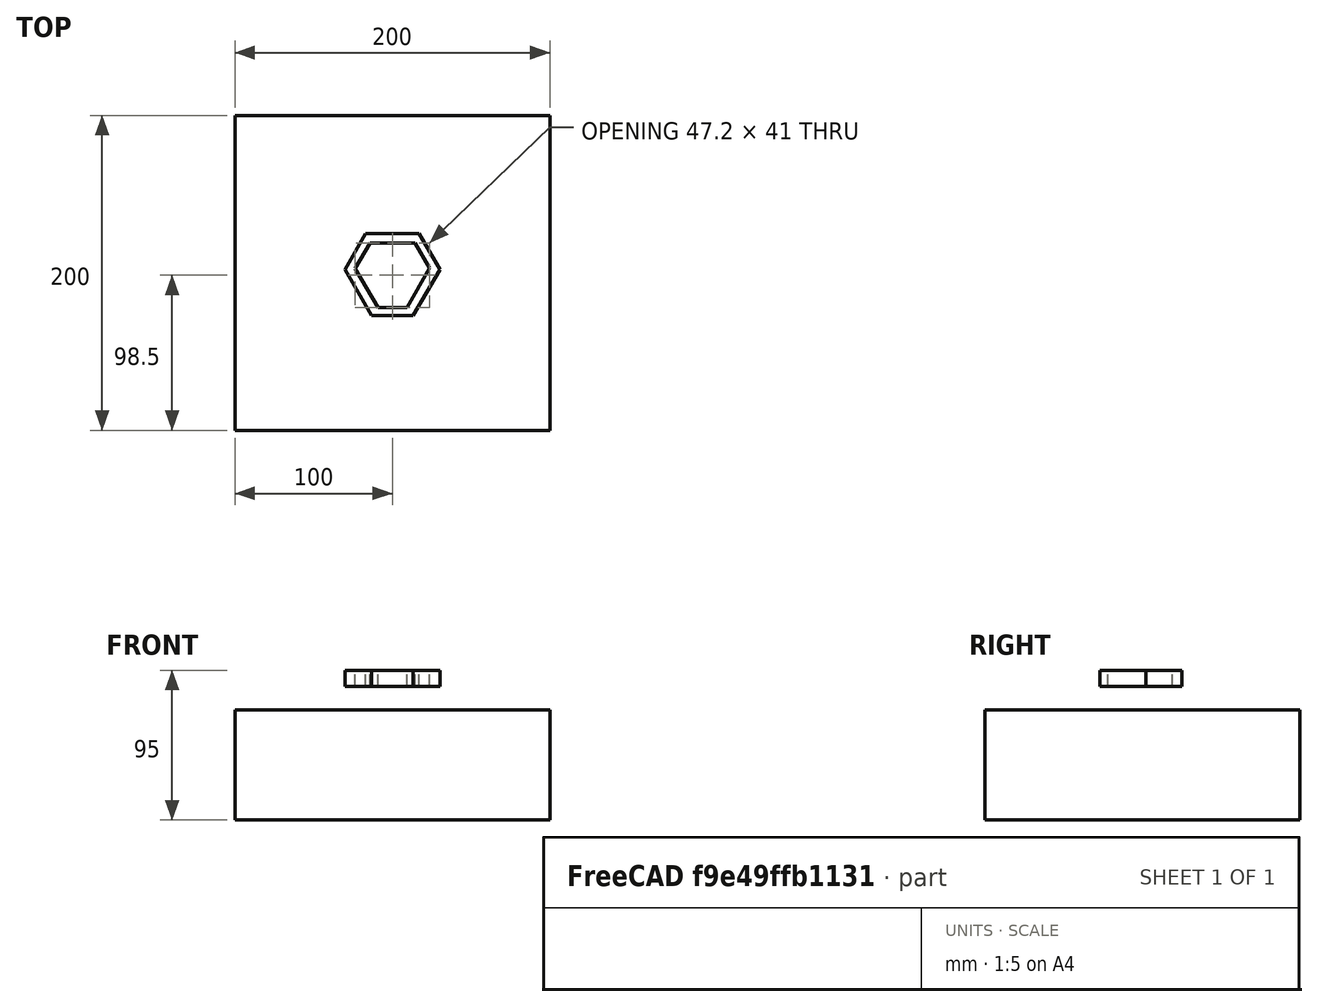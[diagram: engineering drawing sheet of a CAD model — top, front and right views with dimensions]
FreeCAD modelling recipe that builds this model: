
FCSTD DOCUMENT  (FreeCAD 0.19R24366 (Git))
Label: delta_stage_base_coupler
License: All rights reserved
LicenseURL: http://en.wikipedia.org/wiki/All_rights_reserved
objects: Part::Feature×2, Mesh::Feature×1, Part::Box×1, Part::Refine×1, Sketcher::SketchObject×1, Part::Extrusion×1
note: 6 computed .brp shape members not serialized (recipe doc carries the construction recipe); baked Part::Feature solids carry a one-line shape summary decoded from their .brp

FEATURE [Mesh::Feature] delta_stage
FEATURE [Part::Feature] delta_stage001
  shape: bbox 146.9 x 132 x 75.01 mm, 19080 faces, 0 solids (baked)
FEATURE [Part::Feature] delta_stage001_solid  label="delta_stage001 (Solid)"
  shape: bbox 146.9 x 132 x 75.01 mm, 19080 faces (baked)
FEATURE [Part::Box] Box  label="Cube"
  AttacherType = Attacher::AttachEngine3D
  Height = 70
  Length = 200
  Placement = pos=(-100,-100,-10) rot=(0,0,1;0rad)
  Width = 200
FEATURE [Part::Refine] delta_stage001_solid001  label="delta_stage001 (Solid)001"
  Source = -> delta_stage001_solid
FEATURE [Sketcher::SketchObject] Sketch
  FullyConstrained = true
  MapMode = 5
  Placement = pos=(0,0,75) rot=(0,0,1;0rad)
  Support = -> [delta_stage001_solid001]
  sketch-geometry (12):
    g0: LineSegment StartX=9.19671 StartY=-22 StartZ=0 EndX=23.6 EndY=2.94723 EndZ=0
    g1: LineSegment StartX=23.6 StartY=2.94723 StartZ=0 EndX=14.3319 EndY=19 EndZ=0
    g2: LineSegment StartX=14.3319 StartY=19 StartZ=0 EndX=-14.3128 EndY=19 EndZ=0
    g3: LineSegment StartX=-14.3128 StartY=19 StartZ=0 EndX=-23.6 EndY=2.91411 EndZ=0
    g4: LineSegment StartX=-23.6 StartY=2.91411 StartZ=0 EndX=-9.21583 EndY=-22 EndZ=0
    g5: LineSegment StartX=-9.21583 StartY=-22 StartZ=0 EndX=9.19671 EndY=-22 EndZ=0
    g6: LineSegment StartX=-13.2009 StartY=-27.1353 StartZ=0 EndX=13.2029 EndY=-27.1353 EndZ=0
    g7: LineSegment StartX=13.2029 StartY=-27.1353 StartZ=0 EndX=30.1 EndY=2.13139 EndZ=0
    g8: LineSegment StartX=30.1 StartY=2.13139 StartZ=0 EndX=16.8968 EndY=25 EndZ=0
    g9: LineSegment StartX=16.8968 StartY=25 StartZ=0 EndX=-16.8988 EndY=25 EndZ=0
    g10: LineSegment StartX=-16.8988 StartY=25 StartZ=0 EndX=-30.1 EndY=2.13484 EndZ=0
    g11: LineSegment StartX=-30.1 StartY=2.13484 StartZ=0 EndX=-13.2009 EndY=-27.1353 EndZ=0
  constraints (36):
    c: Coincident(g0,g1)
    c: Coincident(g1,g2)
    c: Coincident(g2,g3)
    c: Coincident(g3,g4)
    c: Coincident(g4,g5)
    c: Coincident(g5,g0)
    c: Coincident(g6,g7)
    c: Coincident(g7,g8)
    c: Coincident(g8,g9)
    c: Coincident(g9,g10)
    c: Coincident(g10,g11)
    c: Coincident(g11,g6)
    c: Angle(g3,g2) = 2.0944
    c: Angle(g2,g1) = 2.0944
    c: Angle(g5,g4) = 2.0944
    c: Angle(g0,g5) = 2.0944
    c: DistanceY(g-1,g2) = 19
    c: DistanceY(g-1,g1) = 19
    c: DistanceX(g-1,g0) = 23.6
    c: DistanceX(g3,g-1) = 23.6
    c: DistanceY(g4,g-1) = 22
    c: DistanceY(g0,g-1) = 22
    c: DistanceX(g0,g7) = 6.5
    c: DistanceY(g1,g8) = 6
    c: DistanceY(g2,g9) = 6
    c: Angle(g10,g9) = 2.0944
    c: Angle(g9,g8) = 2.0944
    c: Angle(g7,g6) = 2.0944
    c: Angle(g6,g11) = 2.0944
    c: Angle(g11,g10) = 2.0944
    c: DistanceX(g10,g3) = 6.5
    c: DistanceX(g4) = -9.21583
    c: DistanceY(g0) = 2.94723
    c: DistanceX(g6) = -13.2009
    c: DistanceY(g6) = -27.1353
    c: DistanceY(g7) = 2.13139
FEATURE [Part::Extrusion] Extrude
  Base = -> Sketch
  Dir = (0,0,1)
  DirMode = 2
  FaceMakerClass = Part::FaceMakerBullseye
  LengthFwd = 10
  LengthRev = 0
  Solid = true
  Symmetric = false
